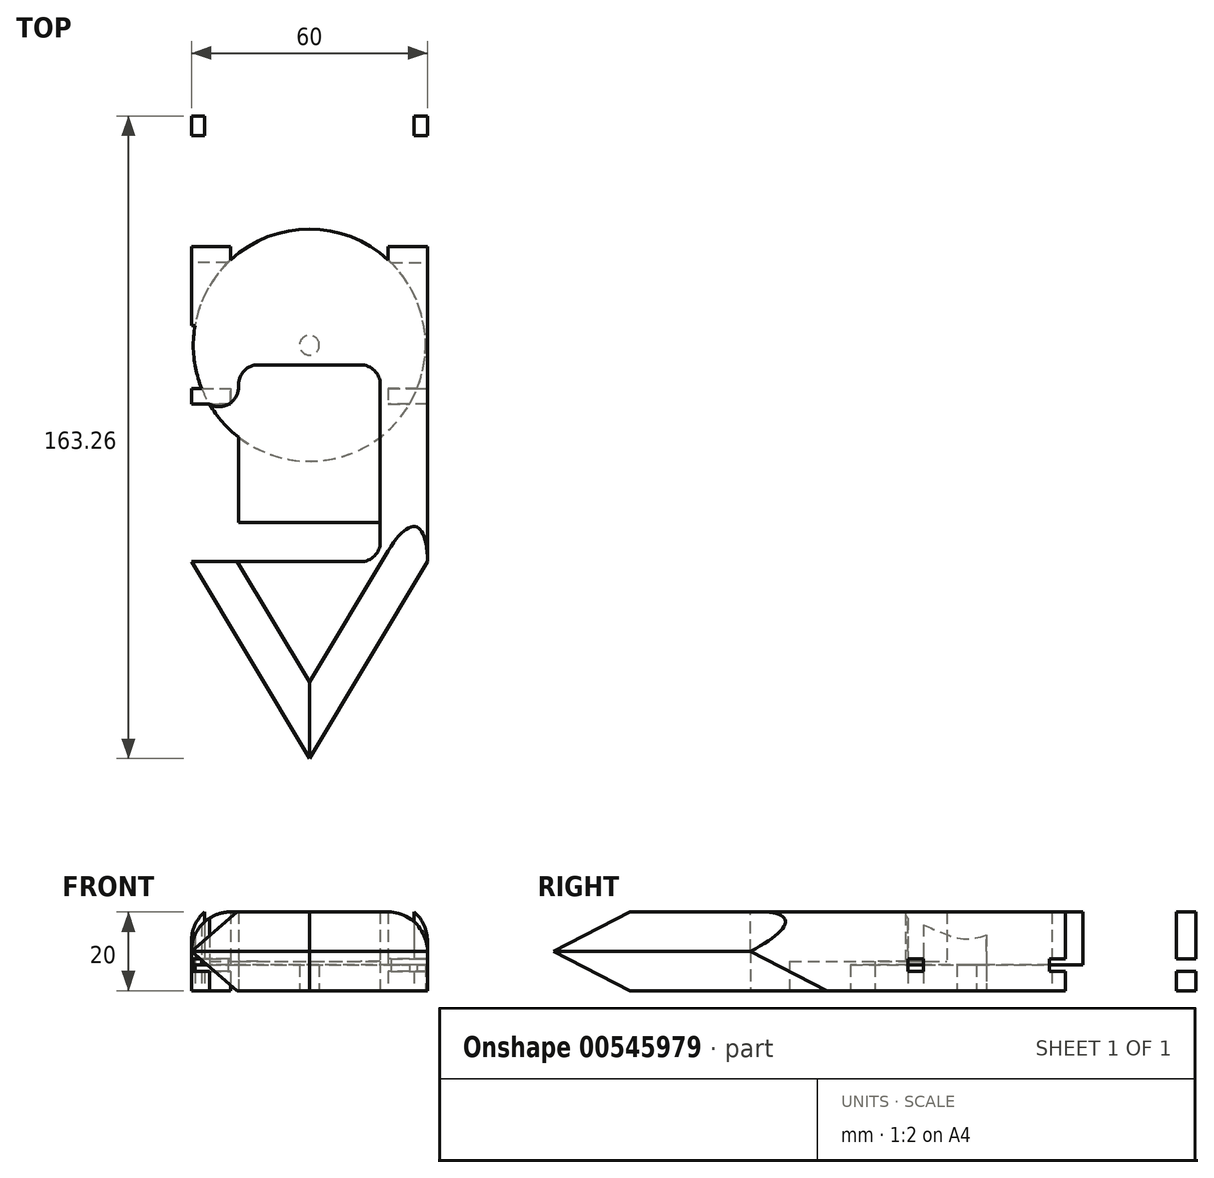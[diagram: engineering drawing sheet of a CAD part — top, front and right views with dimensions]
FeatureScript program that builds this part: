
annotation { "Feature Type Name" : "Feature", "Feature Type Description" : "" }
export const myFeature = defineFeature(function(context is Context, id is Id, definition is map)
    precondition{}
    {
        {
            var Q0;
            Q0=qCreatedBy(makeId("Top.planeOp"),FACE);
            var sketch = newSketch(context, id + "F0", { "sketchPlane" : qUnion([Q0])});
            skLineSegment(sketch, "E0", {"start": v(0, 65.2) * mm, "end": v(0, -54.8) * mm});
            skLineSegment(sketch, "E1", {"start": v(0, -54.8) * mm, "end": v(60, -54.8) * mm});
            skLineSegment(sketch, "E2", {"start": v(30, -54.8) * mm, "end": v(30, -104.8) * mm});
            skLineSegment(sketch, "E3", {"start": v(60, -54.8) * mm, "end": v(60, 65.2) * mm});
            skLineSegment(sketch, "E4", {"start": v(0, 65.2) * mm, "end": v(60, 65.2) * mm});
            skLineSegment(sketch, "E5", {"start": v(30, -54.8) * mm, "end": v(43, -54.8) * mm});
            skLineSegment(sketch, "E6", {"start": v(30, -54.8) * mm, "end": v(12, -54.8) * mm});
            skLineSegment(sketch, "E7", {"start": v(12, -54.8) * mm, "end": v(12, -4.8) * mm});
            skLineSegment(sketch, "E8", {"start": v(30, 65.2) * mm, "end": v(12, 65.2) * mm});
            skLineSegment(sketch, "E9", {"start": v(12, 55.2) * mm, "end": v(12, 75.2) * mm});
            skLineSegment(sketch, "E10", {"start": v(12, 75.2) * mm, "end": v(14.5, 75.2) * mm});
            skLineSegment(sketch, "E11", {"start": v(14.5, 75.2) * mm, "end": v(14.5, 55.2) * mm});
            skLineSegment(sketch, "E12", {"start": v(14.5, 55.2) * mm, "end": v(12, 55.2) * mm});
            skLineSegment(sketch, "E13", {"start": v(30, 65.2) * mm, "end": v(30, 59.57) * mm});
            skLineSegment(sketch, "E14", {"start": v(0, -54.8) * mm, "end": v(0, -49.8) * mm});
            skLineSegment(sketch, "E15.MirrorCS", {"start": v(48, -54.8) * mm, "end": v(48, -4.8) * mm});
            skLineSegment(sketch, "E16", {"start": v(12, -4.8) * mm, "end": v(48, -4.8) * mm});
            skLineSegment(sketch, "E17.MirrorCS", {"start": v(48, 55.2) * mm, "end": v(48, 75.2) * mm});
            skLineSegment(sketch, "E18.MirrorCS", {"start": v(45.5, 75.2) * mm, "end": v(45.5, 55.2) * mm});
            skLineSegment(sketch, "E19.MirrorCS", {"start": v(45.5, 55.2) * mm, "end": v(48, 55.2) * mm});
            skLineSegment(sketch, "E20.MirrorCS", {"start": v(48, 75.2) * mm, "end": v(45.5, 75.2) * mm});
            skLineSegment(sketch, "E21", {"start": v(0, -54.8) * mm, "end": v(30, -104.8) * mm});
            skLineSegment(sketch, "E22", {"start": v(60, -54.8) * mm, "end": v(30, -104.8) * mm});
            skPoint(sketch, "E23", {"position": v(30, 0.2) * mm});
            skCircle(sketch, "E24", {"center": v(30, 0.2) * mm, "radius": 2.5 * mm});
            skCircle(sketch, "E25", {"center": v(30, 0.2) * mm, "radius": 29.5 * mm});
            skLineSegment(sketch, "E26", {"start": v(30, 65.2) * mm, "end": v(35, 65.2) * mm});
            skLineSegment(sketch, "E27", {"start": v(35, 65.2) * mm, "end": v(35, 40.2) * mm});
            skLineSegment(sketch, "E28", {"start": v(35, 40.2) * mm, "end": v(55, 40.2) * mm});
            skLineSegment(sketch, "E29", {"start": v(55, 40.2) * mm, "end": v(55, 65.2) * mm});
            skLineSegment(sketch, "E30.MirrorCS", {"start": v(25, 65.2) * mm, "end": v(25, 40.2) * mm});
            skLineSegment(sketch, "E31.MirrorCS", {"start": v(5, 40.2) * mm, "end": v(5, 65.2) * mm});
            skLineSegment(sketch, "E32.MirrorCS", {"start": v(25, 40.2) * mm, "end": v(5, 40.2) * mm});
            skLineSegment(sketch, "E33", {"start": v(12, -54.8) * mm, "end": v(12, -44.8) * mm});
            skLineSegment(sketch, "E34", {"start": v(12, -44.8) * mm, "end": v(48, -44.8) * mm});
            skLineSegment(sketch, "E35", {"start": v(0, -54.8) * mm, "end": v(0, -14.8) * mm});
            skLineSegment(sketch, "E36", {"start": v(0, -14.8) * mm, "end": v(10, -14.8) * mm});
            skLineSegment(sketch, "E37", {"start": v(10, -14.8) * mm, "end": v(10, -10.8) * mm});
            skLineSegment(sketch, "E38", {"start": v(10, -10.8) * mm, "end": v(0, -10.8) * mm});
            skLineSegment(sketch, "E39", {"start": v(0, -10.8) * mm, "end": v(0, 5.2) * mm});
            skLineSegment(sketch, "E40", {"start": v(0, 5.2) * mm, "end": v(8.88, 5.2) * mm});
            skLineSegment(sketch, "E41.MirrorCS", {"start": v(10, 21.2) * mm, "end": v(0, 21.2) * mm});
            skLineSegment(sketch, "E42.MirrorCS", {"start": v(10, 25.2) * mm, "end": v(10, 21.2) * mm});
            skLineSegment(sketch, "E43.MirrorCS", {"start": v(0, 25.2) * mm, "end": v(10, 25.2) * mm});
            skLineSegment(sketch, "E44.MirrorCS", {"start": v(50, -10.8) * mm, "end": v(60, -10.8) * mm});
            skLineSegment(sketch, "E45.MirrorCS", {"start": v(60, -14.8) * mm, "end": v(50, -14.8) * mm});
            skLineSegment(sketch, "E46.MirrorCS", {"start": v(50, -14.8) * mm, "end": v(50, -10.8) * mm});
            skLineSegment(sketch, "E47.MirrorCS", {"start": v(50, 21.2) * mm, "end": v(60, 21.2) * mm});
            skLineSegment(sketch, "E48.MirrorCS", {"start": v(60, 25.2) * mm, "end": v(50, 25.2) * mm});
            skLineSegment(sketch, "E49.MirrorCS", {"start": v(50, 25.2) * mm, "end": v(50, 21.2) * mm});
            skLineSegment(sketch, "E50", {"start": v(5, 40.2) * mm, "end": v(15, 29.06) * mm});
            skLineSegment(sketch, "E51", {"start": v(15, 29.06) * mm, "end": v(25, 40.2) * mm});
            skLineSegment(sketch, "E52.MirrorCS", {"start": v(45, 29.06) * mm, "end": v(35, 40.2) * mm});
            skLineSegment(sketch, "E53.MirrorCS", {"start": v(55, 40.2) * mm, "end": v(45, 29.06) * mm});
            skLineSegment(sketch, "E54", {"start": v(60, 53.46) * mm, "end": v(56.6, 53.46) * mm});
            skLineSegment(sketch, "E55", {"start": v(56.6, 53.46) * mm, "end": v(56.6, 58.46) * mm});
            skLineSegment(sketch, "E56", {"start": v(56.6, 58.46) * mm, "end": v(60, 58.46) * mm});
            skLineSegment(sketch, "E57.MirrorCS", {"start": v(3.4, 58.46) * mm, "end": v(0, 58.46) * mm});
            skLineSegment(sketch, "E58.MirrorCS", {"start": v(3.4, 53.46) * mm, "end": v(3.4, 58.46) * mm});
            skLineSegment(sketch, "E59.MirrorCS", {"start": v(0, 53.46) * mm, "end": v(3.4, 53.46) * mm});
            skSolve(sketch);
        }
        {
            var Q0;
            {var subQ0=sQuery(id+"F0.wireOp",EDGE,"E44.MirrorCS");var subQ1=sQuery(id+"F0.wireOp",EDGE,"E3");var subQ2=makeQuery(id+"F0.imprint","INTERSECT",VERTEX,{"derivedFrom":[subQ1,subQ0]});Q0=makeQuery(id+"F0.imprint","IMPRINT",FACE,{"disambiguationData":[TD([[makeQuery(id+"F0.imprint","IMPRINT",EDGE,{"disambiguationData":[TD([[subQ2,-1.0]])],"derivedFrom":subQ1}),1.0]])]});}
            var Q1;
            {var subQ0=sQuery(id+"F0.wireOp",EDGE,"E40");var subQ5=sQuery(id+"F0.wireOp",EDGE,"E25");var subQ6=makeQuery(id+"F0.imprint","INTERSECT",VERTEX,{"derivedFrom":[subQ5,subQ0]});Q1=makeQuery(id+"F0.imprint","IMPRINT",FACE,{"disambiguationData":[TD([[makeQuery(id+"F0.imprint","IMPRINT",EDGE,{"disambiguationData":[TD([[subQ6,1.0]])],"derivedFrom":subQ5}),-1.0]])]});}
            var Q2;
            {var subQ3=sQuery(id+"F0.wireOp",EDGE,"E38");var subQ5=sQuery(id+"F0.wireOp",EDGE,"E25");var subQ6=makeQuery(id+"F0.imprint","INTERSECT",VERTEX,{"derivedFrom":[subQ5,subQ3]});Q2=makeQuery(id+"F0.imprint","IMPRINT",FACE,{"disambiguationData":[TD([[makeQuery(id+"F0.imprint","IMPRINT",EDGE,{"disambiguationData":[TD([[subQ6,-1.0]])],"derivedFrom":subQ5}),-1.0]])]});}
            var Q3;
            {var subQ5=sQuery(id+"F0.wireOp",EDGE,"E19.MirrorCS");Q3=makeQuery(id+"F0.imprint","IMPRINT",FACE,{"disambiguationData":[TD([[makeQuery(id+"F0.imprint","IMPRINT",EDGE,{"derivedFrom":subQ5}),1.0]])]});}
            var Q4;
            {var subQ5=sQuery(id+"F0.wireOp",EDGE,"E12");Q4=makeQuery(id+"F0.imprint","IMPRINT",FACE,{"disambiguationData":[TD([[makeQuery(id+"F0.imprint","IMPRINT",EDGE,{"derivedFrom":subQ5}),-1.0]])]});}
            var Q5;
            Q5=makeQuery(id+"F0.imprint","IMPRINT",FACE,{"disambiguationData":[TD([[makeQuery(id+"F0.imprint","IMPRINT",EDGE,{"derivedFrom":sQuery(id+"F0.wireOp",EDGE,"E2")}),1.0]])]});
            var Q6;
            Q6=makeQuery(id+"F0.imprint","IMPRINT",FACE,{"disambiguationData":[TD([[makeQuery(id+"F0.imprint","IMPRINT",EDGE,{"derivedFrom":sQuery(id+"F0.wireOp",EDGE,"E2")}),-1.0]])]});
            var Q7;
            {var subQ17=sQuery(id+"F0.wireOp",EDGE,"E16");Q7=makeQuery(id+"F0.imprint","IMPRINT",FACE,{"disambiguationData":[TD([[makeQuery(id+"F0.imprint","IMPRINT",EDGE,{"derivedFrom":subQ17}),1.0]])]});}
            var Q8;
            Q8=makeQuery(id+"F0.imprint","IMPRINT",FACE,{"disambiguationData":[TD([[makeQuery(id+"F0.imprint","IMPRINT",EDGE,{"derivedFrom":sQuery(id+"F0.wireOp",EDGE,"E24")}),1.0]])]});
            var Q9;
            {var subQ0=sQuery(id+"F0.wireOp",EDGE,"E12");Q9=makeQuery(id+"F0.imprint","IMPRINT",FACE,{"disambiguationData":[TD([[makeQuery(id+"F0.imprint","IMPRINT",EDGE,{"derivedFrom":subQ0}),1.0]])]});}
            var Q10;
            {var subQ0=sQuery(id+"F0.wireOp",EDGE,"E19.MirrorCS");Q10=makeQuery(id+"F0.imprint","IMPRINT",FACE,{"disambiguationData":[TD([[makeQuery(id+"F0.imprint","IMPRINT",EDGE,{"derivedFrom":subQ0}),-1.0]])]});}
            var Q11;
            {var subQ4=sQuery(id+"F0.wireOp",EDGE,"E5");Q11=makeQuery(id+"F0.imprint","IMPRINT",FACE,{"disambiguationData":[TD([[makeQuery(id+"F0.imprint","IMPRINT",EDGE,{"derivedFrom":subQ4}),1.0]])]});}
            var Q12;
            {var subQ0=sQuery(id+"F0.wireOp",EDGE,"E43.MirrorCS");Q12=makeQuery(id+"F0.imprint","IMPRINT",FACE,{"disambiguationData":[TD([[makeQuery(id+"F0.imprint","IMPRINT",EDGE,{"derivedFrom":subQ0}),-1.0]])]});}
            var Q13;
            {var subQ0=sQuery(id+"F0.wireOp",EDGE,"E33");Q13=makeQuery(id+"F0.imprint","IMPRINT",FACE,{"disambiguationData":[TD([[makeQuery(id+"F0.imprint","IMPRINT",EDGE,{"derivedFrom":subQ0}),1.0]])]});}
            var Q14;
            {var subQ5=sQuery(id+"F0.wireOp",EDGE,"E37");Q14=makeQuery(id+"F0.imprint","IMPRINT",FACE,{"disambiguationData":[TD([[makeQuery(id+"F0.imprint","IMPRINT",EDGE,{"derivedFrom":subQ5}),1.0]])]});}
            var Q15;
            {var subQ5=sQuery(id+"F0.wireOp",EDGE,"E39");Q15=makeQuery(id+"F0.imprint","IMPRINT",FACE,{"disambiguationData":[TD([[makeQuery(id+"F0.imprint","IMPRINT",EDGE,{"derivedFrom":subQ5}),-1.0]])]});}
            var Q16;
            {var subQ0=sQuery(id+"F0.wireOp",EDGE,"E15.MirrorCS");var subQ1=sQuery(id+"F0.wireOp",EDGE,"E1");var subQ2=makeQuery(id+"F0.imprint","INTERSECT",VERTEX,{"derivedFrom":[subQ1,subQ0]});Q16=makeQuery(id+"F0.imprint","IMPRINT",FACE,{"disambiguationData":[TD([[makeQuery(id+"F0.imprint","IMPRINT",EDGE,{"disambiguationData":[TD([[subQ2,-1.0]])],"derivedFrom":subQ0}),-1.0]])]});}
            var Q17;
            {var subQ9=sQuery(id+"F0.wireOp",EDGE,"E26");Q17=makeQuery(id+"F0.imprint","IMPRINT",FACE,{"disambiguationData":[TD([[makeQuery(id+"F0.imprint","IMPRINT",EDGE,{"derivedFrom":subQ9}),-1.0]])]});}
            var Q18;
            {var subQ5=sQuery(id+"F0.wireOp",EDGE,"E48.MirrorCS");Q18=makeQuery(id+"F0.imprint","IMPRINT",FACE,{"disambiguationData":[TD([[makeQuery(id+"F0.imprint","IMPRINT",EDGE,{"derivedFrom":subQ5}),1.0]])]});}
            var Q19;
            {var subQ0=sQuery(id+"F0.wireOp",EDGE,"E44.MirrorCS");var subQ1=sQuery(id+"F0.wireOp",EDGE,"E3");var subQ2=makeQuery(id+"F0.imprint","INTERSECT",VERTEX,{"derivedFrom":[subQ1,subQ0]});Q19=makeQuery(id+"F0.imprint","IMPRINT",FACE,{"disambiguationData":[TD([[makeQuery(id+"F0.imprint","IMPRINT",EDGE,{"disambiguationData":[TD([[subQ2,1.0]])],"derivedFrom":subQ1}),1.0]])]});}
            var Q20;
            {var subQ5=sQuery(id+"F0.wireOp",EDGE,"E46.MirrorCS");Q20=makeQuery(id+"F0.imprint","IMPRINT",FACE,{"disambiguationData":[TD([[makeQuery(id+"F0.imprint","IMPRINT",EDGE,{"derivedFrom":subQ5}),-1.0]])]});}
            var Q21;
            {var subQ0=sQuery(id+"F0.wireOp",EDGE,"E42.MirrorCS");var subQ1=sQuery(id+"F0.wireOp",EDGE,"E25");var subQ2=makeQuery(id+"F0.imprint","INTERSECT",VERTEX,{"derivedFrom":[subQ1,subQ0]});Q21=makeQuery(id+"F0.imprint","IMPRINT",FACE,{"disambiguationData":[TD([[makeQuery(id+"F0.imprint","IMPRINT",EDGE,{"disambiguationData":[TD([[subQ2,-1.0]])],"derivedFrom":subQ1}),1.0]])]});}
            var Q22;
            {var subQ0=sQuery(id+"F0.wireOp",EDGE,"E49.MirrorCS");var subQ1=sQuery(id+"F0.wireOp",EDGE,"E25");var subQ2=makeQuery(id+"F0.imprint","INTERSECT",VERTEX,{"derivedFrom":[subQ1,subQ0]});Q22=makeQuery(id+"F0.imprint","IMPRINT",FACE,{"disambiguationData":[TD([[makeQuery(id+"F0.imprint","IMPRINT",EDGE,{"disambiguationData":[TD([[subQ2,1.0]])],"derivedFrom":subQ1}),1.0]])]});}
            var Q23;
            {var subQ0=sQuery(id+"F0.wireOp",EDGE,"E57.MirrorCS");Q23=makeQuery(id+"F0.imprint","IMPRINT",FACE,{"disambiguationData":[TD([[makeQuery(id+"F0.imprint","IMPRINT",EDGE,{"derivedFrom":subQ0}),1.0]])]});}
            var Q24;
            {var subQ0=sQuery(id+"F0.wireOp",EDGE,"E54");Q24=makeQuery(id+"F0.imprint","IMPRINT",FACE,{"disambiguationData":[TD([[makeQuery(id+"F0.imprint","IMPRINT",EDGE,{"derivedFrom":subQ0}),-1.0]])]});}
            extrude(context, id + "F1", {"entities" : qUnion([Q0, Q1, Q2, Q3, Q4, Q5, Q6, Q7, Q8, Q9, Q10, Q11, Q12, Q13, Q14, Q15, Q16, Q17, Q18, Q19, Q20, Q21, Q22, Q23, Q24]), "depth" : 20 * mm, "offsetDistance" : 25 * mm});
        }
        {
            var Q0;
            {var subQ0=sQuery(id+"F0.wireOp",EDGE,"E16");Q0=makeQuery(id+"F0.imprint","IMPRINT",FACE,{"disambiguationData":[TD([[makeQuery(id+"F0.imprint","IMPRINT",EDGE,{"derivedFrom":subQ0}),-1.0]])]});}
            var Q1;
            {var subQ0=sQuery(id+"F0.wireOp",EDGE,"E34");Q1=makeQuery(id+"F0.imprint","IMPRINT",FACE,{"disambiguationData":[TD([[makeQuery(id+"F0.imprint","IMPRINT",EDGE,{"derivedFrom":subQ0}),1.0]])]});}
            extrude(context, id + "F2", {"entities" : qUnion([Q0, Q1]), "operationType" : NewBodyOperationType.ADD, "depth" : 7.5 * mm, "offsetDistance" : 25 * mm});
        }
        {
            var Q0;
            {var subQ0=sQuery(id+"F0.wireOp",EDGE,"E16");Q0=makeQuery(id+"F0.imprint","IMPRINT",FACE,{"disambiguationData":[TD([[makeQuery(id+"F0.imprint","IMPRINT",EDGE,{"derivedFrom":subQ0}),-1.0]])]});}
            var Q1;
            {var subQ15=sQuery(id+"F0.wireOp",EDGE,"E16");Q1=makeQuery(id+"F0.imprint","IMPRINT",FACE,{"disambiguationData":[TD([[makeQuery(id+"F0.imprint","IMPRINT",EDGE,{"derivedFrom":subQ15}),1.0]])]});}
            var Q2;
            {var subQ5=sQuery(id+"F0.wireOp",EDGE,"E37");Q2=makeQuery(id+"F0.imprint","IMPRINT",FACE,{"disambiguationData":[TD([[makeQuery(id+"F0.imprint","IMPRINT",EDGE,{"derivedFrom":subQ5}),1.0]])]});}
            var Q3;
            {var subQ5=sQuery(id+"F0.wireOp",EDGE,"E46.MirrorCS");Q3=makeQuery(id+"F0.imprint","IMPRINT",FACE,{"disambiguationData":[TD([[makeQuery(id+"F0.imprint","IMPRINT",EDGE,{"derivedFrom":subQ5}),-1.0]])]});}
            var Q4;
            {var subQ0=sQuery(id+"F0.wireOp",EDGE,"E42.MirrorCS");var subQ1=sQuery(id+"F0.wireOp",EDGE,"E25");var subQ2=makeQuery(id+"F0.imprint","INTERSECT",VERTEX,{"derivedFrom":[subQ1,subQ0]});Q4=makeQuery(id+"F0.imprint","IMPRINT",FACE,{"disambiguationData":[TD([[makeQuery(id+"F0.imprint","IMPRINT",EDGE,{"disambiguationData":[TD([[subQ2,-1.0]])],"derivedFrom":subQ1}),1.0]])]});}
            var Q5;
            {var subQ0=sQuery(id+"F0.wireOp",EDGE,"E49.MirrorCS");var subQ1=sQuery(id+"F0.wireOp",EDGE,"E25");var subQ2=makeQuery(id+"F0.imprint","INTERSECT",VERTEX,{"derivedFrom":[subQ1,subQ0]});Q5=makeQuery(id+"F0.imprint","IMPRINT",FACE,{"disambiguationData":[TD([[makeQuery(id+"F0.imprint","IMPRINT",EDGE,{"disambiguationData":[TD([[subQ2,1.0]])],"derivedFrom":subQ1}),1.0]])]});}
            extrude(context, id + "F3", {"entities" : qUnion([Q0, Q1, Q2, Q3, Q4, Q5]), "operationType" : NewBodyOperationType.REMOVE, "depth" : 6.5 * mm, "offsetDistance" : 25 * mm});
        }
        {
            var Q0;
            Q0=makeQuery(id+"F1.opExtrude","SWEPT_EDGE",EDGE,{"disambiguationData":[OSD([sQuery(id+"F0.wireOp",EDGE,"E15.MirrorCS"),sQuery(id+"F0.wireOp",EDGE,"E16")])]});
            var Q1;
            Q1=makeQuery(id+"F1.opExtrude","SWEPT_EDGE",EDGE,{"disambiguationData":[OSD([sQuery(id+"F0.wireOp",EDGE,"E7"),sQuery(id+"F0.wireOp",EDGE,"E16")])]});
            var Q2;
            Q2=makeQuery(id+"F1.opExtrude","SWEPT_EDGE",EDGE,{"disambiguationData":[OSD([sQuery(id+"F0.wireOp",EDGE,"E1"),sQuery(id+"F0.wireOp",EDGE,"E6"),sQuery(id+"F0.wireOp",EDGE,"E7")])]});
            var Q3;
            Q3=makeQuery(id+"F1.opExtrude","SWEPT_EDGE",EDGE,{"disambiguationData":[OSD([sQuery(id+"F0.wireOp",EDGE,"E1"),sQuery(id+"F0.wireOp",EDGE,"E15.MirrorCS")])]});
            var Q4;
            Q4=makeQuery(id+"F1.opExtrude","SWEPT_EDGE",EDGE,{"disambiguationData":[OSD([sQuery(id+"F0.wireOp",EDGE,"E7"),sQuery(id+"F0.wireOp",EDGE,"E33"),sQuery(id+"F0.wireOp",EDGE,"E34")])]});
            fillet(context, id + "F4", {"entities" : qUnion([Q0, Q1, Q2, Q3, Q4]), "radius" : 5 * mm, "tangentPropagation" : true, "allowEdgeOverflow" : false});
        }
        {
            var Q0;
            Q0=makeQuery(id+"F1.opExtrude","CAP_EDGE",EDGE,{"disambiguationData":[OSD([sQuery(id+"F0.wireOp",EDGE,"E21")])],"isStart":false});
            var Q1;
            Q1=makeQuery(id+"F1.opExtrude","CAP_EDGE",EDGE,{"disambiguationData":[OSD([sQuery(id+"F0.wireOp",EDGE,"E22")])],"isStart":false});
            chamfer(context, id + "F5", {"entities" : qUnion([Q0, Q1]), "width" : 10 * mm, "tangentPropagation" : true});
        }
        {
            var Q0;
            Q0=makeQuery(id+"F1.opExtrude","CAP_EDGE",EDGE,{"disambiguationData":[OSD([sQuery(id+"F0.wireOp",EDGE,"E22")])],"isStart":true});
            var Q1;
            Q1=makeQuery(id+"F1.opExtrude","CAP_EDGE",EDGE,{"disambiguationData":[OSD([sQuery(id+"F0.wireOp",EDGE,"E21")])],"isStart":true});
            chamfer(context, id + "F6", {"entities" : qUnion([Q0, Q1]), "width" : 10 * mm, "tangentPropagation" : true});
        }
        {
            var Q0;
            Q0=makeQuery(id+"F1.opExtrude","CAP_EDGE",EDGE,{"disambiguationData":[OSD([sQuery(id+"F0.wireOp",EDGE,"E3")])],"isStart":false});
            var Q1;
            Q1=makeQuery(id+"F1.opExtrude","CAP_EDGE",EDGE,{"disambiguationData":[OSD([sQuery(id+"F0.wireOp",EDGE,"E0"),sQuery(id+"F0.wireOp",EDGE,"E14")])],"isStart":false});
            fillet(context, id + "F7", {"entities" : qUnion([Q0, Q1]), "radius" : 10 * mm, "tangentPropagation" : true, "allowEdgeOverflow" : false});
        }
        {
            var Q0;
            Q0=makeQuery(id+"F1.opExtrude","CAP_EDGE",EDGE,{"disambiguationData":[OSD([sQuery(id+"F0.wireOp",EDGE,"E4"),sQuery(id+"F0.wireOp",EDGE,"E8")])],"isStart":false});
            var Q1;
            Q1=makeQuery(id+"F1.opExtrude","CAP_EDGE",EDGE,{"disambiguationData":[OSD([sQuery(id+"F0.wireOp",EDGE,"E4"),sQuery(id+"F0.wireOp",EDGE,"E8")])],"isStart":true});
            chamfer(context, id + "F8", {"entities" : qUnion([Q0, Q1]), "width" : 7.5 * mm, "tangentPropagation" : true});
        }
        {
            var Q0;
            {var subQ0=sQuery(id+"F0.wireOp",EDGE,"E12");Q0=makeQuery(id+"F0.imprint","IMPRINT",FACE,{"disambiguationData":[TD([[makeQuery(id+"F0.imprint","IMPRINT",EDGE,{"derivedFrom":subQ0}),1.0]])]});}
            var Q1;
            {var subQ5=sQuery(id+"F0.wireOp",EDGE,"E10");Q1=makeQuery(id+"F0.imprint","IMPRINT",FACE,{"disambiguationData":[TD([[makeQuery(id+"F0.imprint","IMPRINT",EDGE,{"derivedFrom":subQ5}),-1.0]])]});}
            var Q2;
            {var subQ5=sQuery(id+"F0.wireOp",EDGE,"E12");Q2=makeQuery(id+"F0.imprint","IMPRINT",FACE,{"disambiguationData":[TD([[makeQuery(id+"F0.imprint","IMPRINT",EDGE,{"derivedFrom":subQ5}),-1.0]])]});}
            var Q3;
            {var subQ0=sQuery(id+"F0.wireOp",EDGE,"E19.MirrorCS");Q3=makeQuery(id+"F0.imprint","IMPRINT",FACE,{"disambiguationData":[TD([[makeQuery(id+"F0.imprint","IMPRINT",EDGE,{"derivedFrom":subQ0}),-1.0]])]});}
            var Q4;
            {var subQ5=sQuery(id+"F0.wireOp",EDGE,"E19.MirrorCS");Q4=makeQuery(id+"F0.imprint","IMPRINT",FACE,{"disambiguationData":[TD([[makeQuery(id+"F0.imprint","IMPRINT",EDGE,{"derivedFrom":subQ5}),1.0]])]});}
            var Q5;
            {var subQ5=sQuery(id+"F0.wireOp",EDGE,"E20.MirrorCS");Q5=makeQuery(id+"F0.imprint","IMPRINT",FACE,{"disambiguationData":[TD([[makeQuery(id+"F0.imprint","IMPRINT",EDGE,{"derivedFrom":subQ5}),1.0]])]});}
            extrude(context, id + "F9", {"entities" : qUnion([Q0, Q1, Q2, Q3, Q4, Q5]), "operationType" : NewBodyOperationType.REMOVE, "depth" : 20 * mm, "offsetDistance" : 25 * mm});
        }
        {
            var Q0;
            {var subQ0=sQuery(id+"F0.wireOp",EDGE,"E43.MirrorCS");Q0=makeQuery(id+"F0.imprint","IMPRINT",FACE,{"disambiguationData":[TD([[makeQuery(id+"F0.imprint","IMPRINT",EDGE,{"derivedFrom":subQ0}),-1.0]])]});}
            var Q1;
            {var subQ5=sQuery(id+"F0.wireOp",EDGE,"E48.MirrorCS");Q1=makeQuery(id+"F0.imprint","IMPRINT",FACE,{"disambiguationData":[TD([[makeQuery(id+"F0.imprint","IMPRINT",EDGE,{"derivedFrom":subQ5}),1.0]])]});}
            var Q2;
            {var subQ5=sQuery(id+"F0.wireOp",EDGE,"E37");Q2=makeQuery(id+"F0.imprint","IMPRINT",FACE,{"disambiguationData":[TD([[makeQuery(id+"F0.imprint","IMPRINT",EDGE,{"derivedFrom":subQ5}),1.0]])]});}
            var Q3;
            {var subQ3=sQuery(id+"F0.wireOp",EDGE,"E38");var subQ5=sQuery(id+"F0.wireOp",EDGE,"E25");var subQ6=makeQuery(id+"F0.imprint","INTERSECT",VERTEX,{"derivedFrom":[subQ5,subQ3]});Q3=makeQuery(id+"F0.imprint","IMPRINT",FACE,{"disambiguationData":[TD([[makeQuery(id+"F0.imprint","IMPRINT",EDGE,{"disambiguationData":[TD([[subQ6,-1.0]])],"derivedFrom":subQ5}),-1.0]])]});}
            var Q4;
            {var subQ5=sQuery(id+"F0.wireOp",EDGE,"E46.MirrorCS");Q4=makeQuery(id+"F0.imprint","IMPRINT",FACE,{"disambiguationData":[TD([[makeQuery(id+"F0.imprint","IMPRINT",EDGE,{"derivedFrom":subQ5}),-1.0]])]});}
            var Q5;
            {var subQ0=sQuery(id+"F0.wireOp",EDGE,"E44.MirrorCS");var subQ1=sQuery(id+"F0.wireOp",EDGE,"E3");var subQ2=makeQuery(id+"F0.imprint","INTERSECT",VERTEX,{"derivedFrom":[subQ1,subQ0]});Q5=makeQuery(id+"F0.imprint","IMPRINT",FACE,{"disambiguationData":[TD([[makeQuery(id+"F0.imprint","IMPRINT",EDGE,{"disambiguationData":[TD([[subQ2,1.0]])],"derivedFrom":subQ1}),1.0]])]});}
            var Q6;
            {var subQ0=sQuery(id+"F0.wireOp",EDGE,"E54");Q6=makeQuery(id+"F0.imprint","IMPRINT",FACE,{"disambiguationData":[TD([[makeQuery(id+"F0.imprint","IMPRINT",EDGE,{"derivedFrom":subQ0}),-1.0]])]});}
            var Q7;
            {var subQ0=sQuery(id+"F0.wireOp",EDGE,"E57.MirrorCS");Q7=makeQuery(id+"F0.imprint","IMPRINT",FACE,{"disambiguationData":[TD([[makeQuery(id+"F0.imprint","IMPRINT",EDGE,{"derivedFrom":subQ0}),1.0]])]});}
            extrude(context, id + "F10", {"entities" : qUnion([Q0, Q1, Q2, Q3, Q4, Q5, Q6, Q7]), "operationType" : NewBodyOperationType.REMOVE, "depth" : 8.14 * mm, "offsetDistance" : 25 * mm, "hasSecondDirection" : true, "secondDirectionOppositeDirection" : false, "secondDirectionDepth" : 4.9 * mm});
        }
    });
